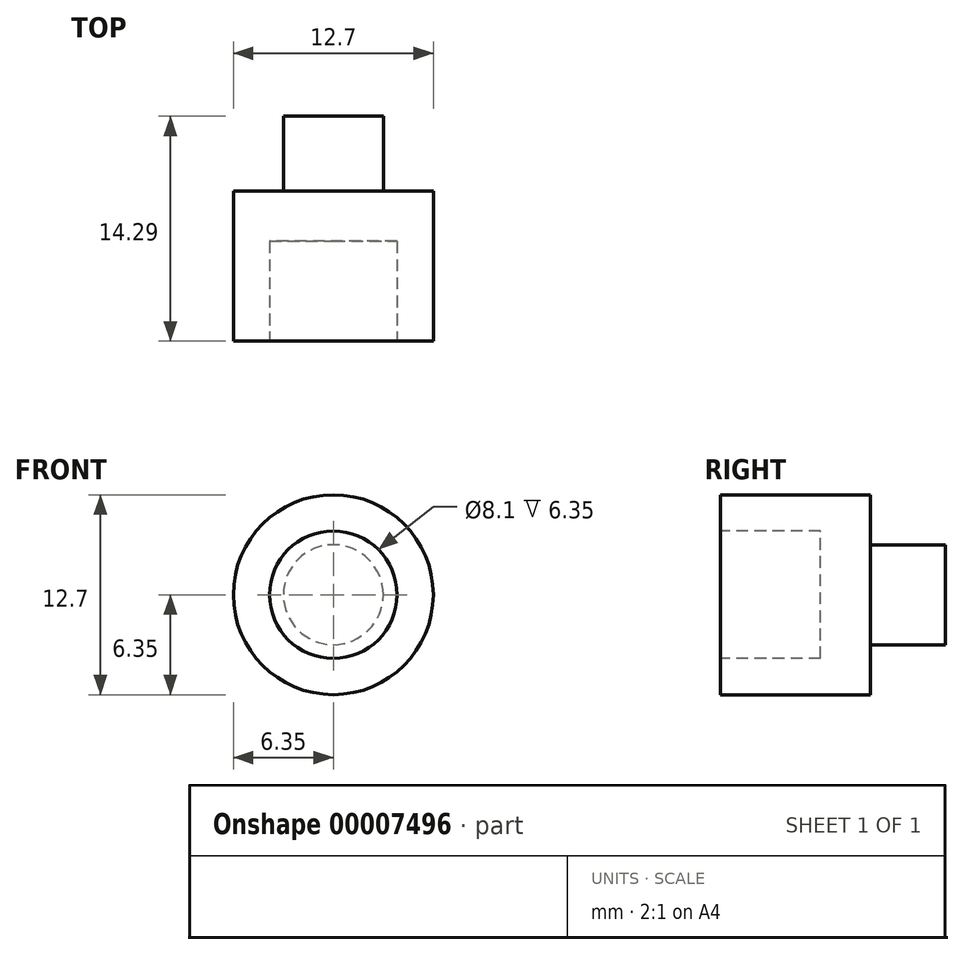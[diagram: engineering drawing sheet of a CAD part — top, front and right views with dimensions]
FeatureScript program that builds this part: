
annotation { "Feature Type Name" : "Feature", "Feature Type Description" : "" }
export const myFeature = defineFeature(function(context is Context, id is Id, definition is map)
    precondition{}
    {
        {
            var Q0;
            Q0=qCreatedBy(makeId("Front.planeOp"),FACE);
            var sketch = newSketch(context, id + "F0", { "sketchPlane" : qUnion([Q0])});
            skCircle(sketch, "E0", {"center": v(0, 0) * mm, "radius": 3.18 * mm});
            skSolve(sketch);
        }
        {
            var Q0;
            Q0 = qSketchRegion(id + "F0", true);
            extrude(context, id + "F1", {"entities" : qUnion([Q0]), "depth" : 4.76 * mm});
        }
        {
            var Q0;
            Q0=makeQuery(id+"F1.opExtrude","CAP_FACE",FACE,{"disambiguationData":[OSD([sQuery(id+"F0.wireOp",EDGE,"E0")])],"isStart":false});
            var sketch = newSketch(context, id + "F2", { "sketchPlane" : qUnion([Q0])});
            skCircle(sketch, "E1", {"center": v(0, 0) * mm, "radius": 6.35 * mm});
            skSolve(sketch);
        }
        {
            var Q0;
            Q0 = qSketchRegion(id + "F2", true);
            extrude(context, id + "F3", {"entities" : qUnion([Q0]), "operationType" : NewBodyOperationType.ADD, "depth" : 9.52 * mm});
        }
        {
            var Q0;
            Q0=makeQuery(id+"F3.opExtrude","CAP_FACE",FACE,{"disambiguationData":[OSD([sQuery(id+"F2.wireOp",EDGE,"E1")])],"isStart":false});
            var sketch = newSketch(context, id + "F4", { "sketchPlane" : qUnion([Q0])});
            skCircle(sketch, "E2", {"center": v(0, 0) * mm, "radius": 4.05 * mm});
            skSolve(sketch);
        }
        {
            var Q0;
            Q0 = qSketchRegion(id + "F4", true);
            extrude(context, id + "F5", {"entities" : qUnion([Q0]), "operationType" : NewBodyOperationType.REMOVE, "oppositeDirection" : true, "depth" : 6.35 * mm});
        }
    });
